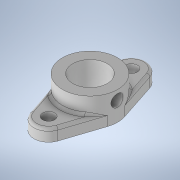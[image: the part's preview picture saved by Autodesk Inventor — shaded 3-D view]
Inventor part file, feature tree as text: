
AUTODESK INVENTOR PART (.ipt)
format: ipt  version: 2021 (Build 250183000, 183)  size: 200,704 bytes
history: native  units: mm
features: sketch x5, hole x3, other x2, extrude x2, fillet x1
ambient origin geometry x8: Origin, YZ Plane, XZ Plane, XY Plane, X Axis, Y Axis, Z Axis, Center Point
bodies: Body1 (feature_tree)
feature tree (13):
  other  "Sólido1"
  extrude  "Extrusão1"  Depth=17.0mm
  extrude  "Extrusão2"  Depth=14.0mm TaperAngle=0.0deg
  hole  "Furo1"  [1 undecoded]
  hole  "Furo2"  [1 undecoded]
  other  "Plano de trabalho1"
  hole  "Furo3"  [1 undecoded]
  fillet  "Arredondamento1"  [1 undecoded]
  sketch  "Esboço1"  dims[d0=32.0mm d1=17.0mm]
  sketch  "Esboço2"  dims[d2=96.0mm d3=14.0mm d4=0.0mm]
  sketch  "Esboço3"  dims[d5=19.0mm d6=0.0mm]
  sketch  "Esboço4"  dims[d7=14.0mm d8=6.0mm d9=4.0mm d10=2.0mm d11=90.0deg d12=8.0mm d13=20.594885mm]
  sketch  "Esboço5"  dims[d14=40.0mm d15=6.0mm d16=4.0mm d17=2.0mm d18=90.0deg d19=8.0mm d20=20.594885mm d21=11.0mm d22=14.0mm d23=6.0mm d24=4.0mm d25=2.0mm d26=90.0deg d27=8.0mm d28=0.0mm d29=3.0mm]
note: 4 required parameter values undecoded (feature->parameter linkage not recoverable at this tier; creation-order binding heuristic only, values carry confidence <= 0.55)
